# Revit family: Commercial_Shower_System-American_Standard-TU662SG211.002
name_source: partatom
category: Plumbing Fixtures
units: mm (PartAtom-declared; Revit-internal decimal feet)

## family parameters
Cut with Voids When Loaded = No
Host = Face
OmniClass Number = 23.45.05.14.17
OmniClass Title = Showers
Part Type = Normal
Room Calculation Point = No
Round Connector Dimension = Use Diameter
Shared = Yes

## types (1)
- TU662SG211.002
    1660.400 In-Line Vacuum Breaker = Yes
    1660.766 3-Function Hand Shower with non-positive shut-off = Yes
    1662.236 36" Slide Bar = Yes
    8888.035 59" Metal Hose = Yes
    8888.037 Wall Supply = Yes
    ADA Compliant = Yes
    Assembly Code = D2010710
    CEC Compliant = Yes
    CW Connection = Yes
    CWFU = 3
    CalGreen Compliant = Yes
    Cold Water Connection Diameter = 1/2"
    Connection Diameter = 1/2"
    Default Elevation = 0"
    Description = Commercial Shower System Trim Kit 1.5 gpm/5.7 Lpm with 36-Inch Slide-Grab Bar and Hand Shower
    EPA WaterSense® Certified = Yes
    Finish = Metal-American Standard-002-Polished Chrome
    Flash Rough-In Valve = Sold Separately
    Flow Rate = 1.5 gpm/5.7 Lpm
    HW Connection = Yes
    HWFU = 3
    Hot Water Connection Diameter = 1/2"
    IAPMO Compliance = These products meets or exceeds ASSE 1016, ASME A112.18.1016, CSA B125.16, ASME A112.18.1 & CSA B125.1
    Installation Instruction Link = https://americanstandard.box.com
    Installation Type = Wall Mounted
    Manufacturer = American Standard
    Material = Metal-American Standard-002-Polished Chrome
    Model = TU662SG211.002
    Price = Prices may vary. Please consult Manufacturer Representative for most up-to-date price list.
    Product Documentation Link = https://americanstandard.box.com
    Product Page URL = https://www.americanstandard-us.com
    TU385500WD Reliant3 Valve Only Trim = Yes
    Tempered Water Connection = Yes
    URL = https://www.americanstandard-us.com
    Vent Connection = No
    WFU = 4
    Waste Connection = No

## geometry (parser evidence)
native form markers: Sweep x18
no freeform markers — native parametric forms only
